# Revit family: S-9604-PLR
name_source: partatom
category: Plumbing Fixtures
units: mm (PartAtom-declared; Revit-internal decimal feet)

## family parameters
Cut with Voids When Loaded = No
Host = Face
OmniClass Number = 23.65.70.11.11
OmniClass Title = Fixtures for Liquids
Part Type = Normal
Room Calculation Point = No
Round Connector Dimension = Use Diameter
Shared = No

## types (8) — shared parameters
CW Connection = No
HW Connection = No
Vent Connection = No
Waste Connection = No
z GPM GPM = 0.000 GPM
z Has Rebuild Kit Trim Only = No
z Has Trim = No
zero-valued in all types: Default Elevation, z  Showerhead, z .5 Inch Female Connections, z Error Box Depth, z Error Box Height, z Error Box Width, z Flow Rate, z GPM Number, z Integral Service Stops, z Offset, z Overall Depth, z Overall Height, z Overall Width, z Pipe Radius, z Reverse Core, z Slip On Tub, z Type, z Type Finish, z Type GPM, z Type Model, z Wide Lever

## per-type parameters (varying)
| type | Gallons Per Minute | Product Material | z Has .5 Inch Female Connections | z Has 1.5 GPM Flow Restrictor | z Has 2.0 GPM Flow Restrictor | z Has Check Stops | z Has Integral Service Stops | z Has Reverse Core | z Has Showerhead | z Has Slip On Tub Spout | z Has Volume Control | z Has Wide Lever Handle | z Visibility |
| 1.2 GPM Flow Restrictor, Chrome | 1.200 GPM | Chrome - Symmons - Polished | Yes | Yes | Yes | Yes | Yes | Yes | Yes | Yes | Yes | Yes | Yes |
| 1.2 GPM Flow Restrictor, Satin Nickel | 1.200 GPM | Nickel - Symmons - Satin | Yes | Yes | Yes | Yes | Yes | Yes | Yes | Yes | Yes | Yes | Yes |
| 1.5 GPM Flow Restrictor, Satin Nickel | 1.500 GPM | Nickel - Symmons - Satin | Yes | Yes | Yes | Yes | Yes | Yes | Yes | Yes | Yes | Yes | Yes |
| 1.75 GPM Flow Restrictor, Satin Nickel | 1.750 GPM | Nickel - Symmons - Satin | Yes | Yes | Yes | Yes | Yes | Yes | Yes | Yes | Yes | Yes | Yes |
| 2.0 GPM Flow Restrictor, Satin Nickel | 2.000 GPM | Nickel - Symmons - Satin | No | No | No | No | No | No | No | No | No | No | No |
| 1.5 GPM Flow Restrictor, Chrome | 1.500 GPM | Chrome - Symmons - Polished | Yes | Yes | Yes | Yes | Yes | Yes | Yes | Yes | Yes | Yes | Yes |
| 1.75 GPM Flow Restrictor, Chrome | 1.750 GPM | Chrome - Symmons - Polished | Yes | Yes | Yes | Yes | Yes | Yes | Yes | Yes | Yes | Yes | Yes |
| 2.0 GPM Flow Restrictor, Chrome | 2.000 GPM | Chrome - Symmons - Polished | Yes | Yes | Yes | Yes | Yes | Yes | Yes | Yes | Yes | Yes | Yes |

## geometry (parser evidence)
native form markers: Blend x8, Sweep x8
no freeform markers — native parametric forms only
